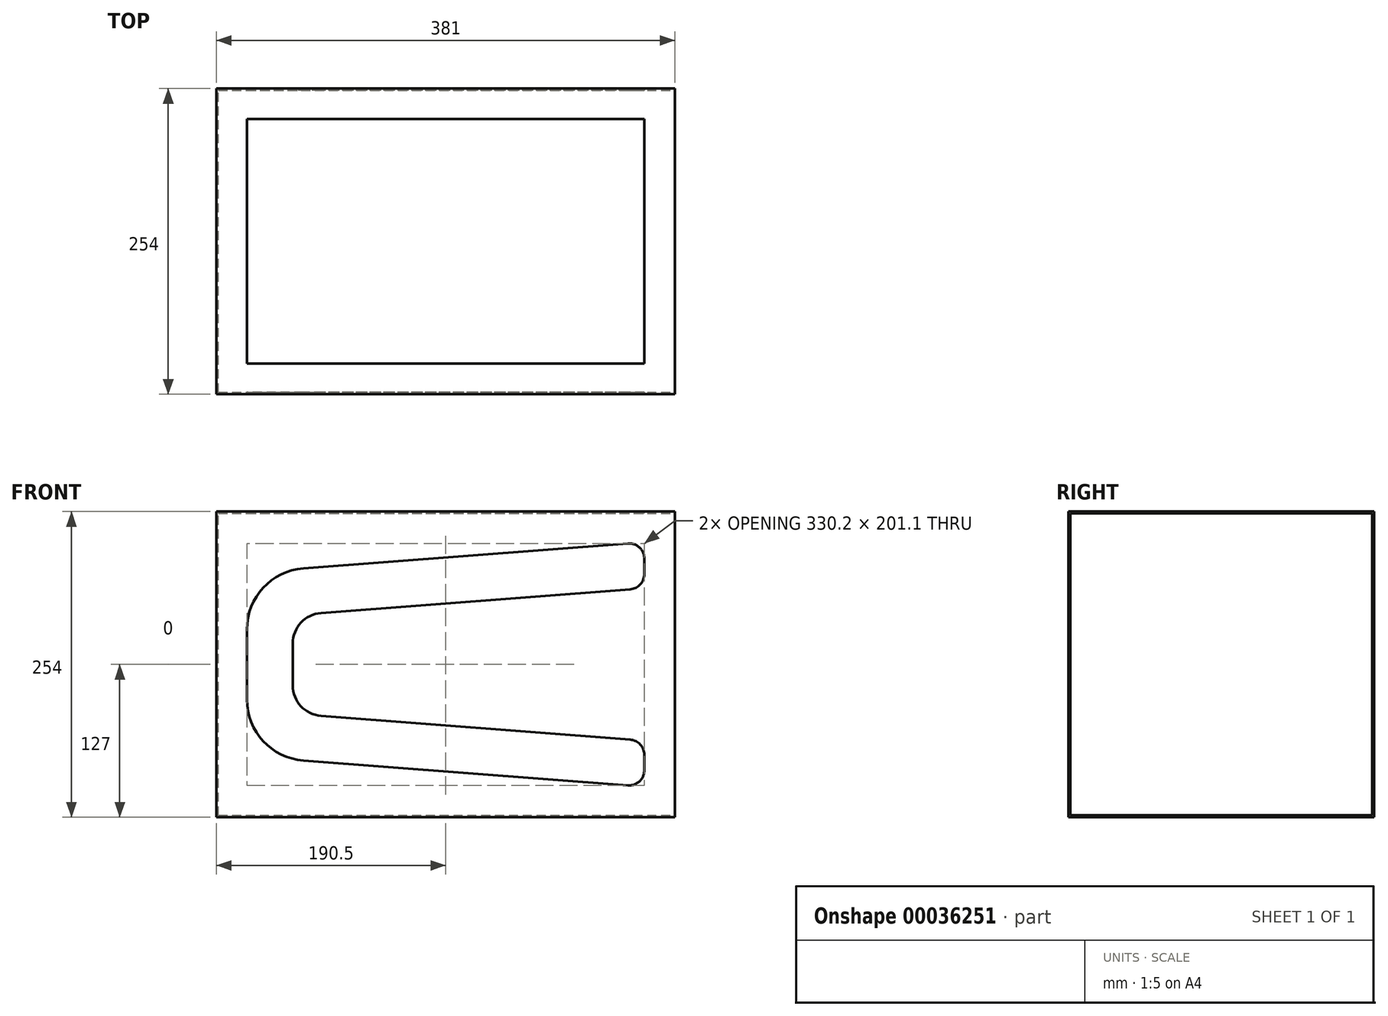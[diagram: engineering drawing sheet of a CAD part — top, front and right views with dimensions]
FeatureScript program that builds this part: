
annotation { "Feature Type Name" : "Feature", "Feature Type Description" : "" }
export const myFeature = defineFeature(function(context is Context, id is Id, definition is map)
    precondition{}
    {
        {
            var Q0;
            Q0=qCreatedBy(makeId("Front.planeOp"),FACE);
            var sketch = newSketch(context, id + "F0", { "sketchPlane" : qUnion([Q0])});
            skLineSegment(sketch, "E0.bottom", {"start": v(0, 0) * mm, "end": v(381, 0) * mm});
            skLineSegment(sketch, "E0.top", {"start": v(0, 254) * mm, "end": v(381, 254) * mm});
            skLineSegment(sketch, "E0.left", {"start": v(0, 0) * mm, "end": v(0, 254) * mm});
            skLineSegment(sketch, "E0.right", {"start": v(381, 0) * mm, "end": v(381, 254) * mm});
            skSolve(sketch);
        }
        {
            var Q0;
            Q0=qSketchRegion(id+"F0",true);
            extrude(context, id + "F1", {"entities" : qUnion([Q0]), "depth" : 254 * mm});
        }
        {
            var Q0;
            Q0=makeQuery(id+"F1.opExtrude","SWEPT_FACE",FACE,{"disambiguationData":[OSD([sQuery(id+"F0.wireOp",EDGE,"E0.right")])]});
            shell(context, id + "F2", {"entities" : qUnion([Q0]), "thickness" : 1.59 * mm});
        }
        {
            var Q0;
            Q0=makeQuery(id+"F1.opExtrude","CAP_FACE",FACE,{"disambiguationData":[OSD([sQuery(id+"F0.wireOp",EDGE,"E0.bottom"),sQuery(id+"F0.wireOp",EDGE,"E0.top"),sQuery(id+"F0.wireOp",EDGE,"E0.left"),sQuery(id+"F0.wireOp",EDGE,"E0.right")])],"isStart":false});
            var sketch = newSketch(context, id + "F3", { "sketchPlane" : qUnion([Q0])});
            skLineSegment(sketch, "E1.left", {"start": v(25.4, 97.84) * mm, "end": v(25.4, 156.16) * mm});
            skLineSegment(sketch, "E1.right", {"start": v(355.6, 39.11) * mm, "end": v(355.6, 51.85) * mm});
            skLineSegment(sketch, "E2", {"start": v(341.93, 227.55) * mm, "end": v(72.3, 206.8) * mm});
            skPoint(sketch, "E1.top.start.orphan", {"position": v(25.4, 228.6) * mm});
            skLineSegment(sketch, "E3.0", {"start": v(343.87, 189.49) * mm, "end": v(86.95, 169.72) * mm});
            skLineSegment(sketch, "E4", {"start": v(341.93, 26.45) * mm, "end": v(72.3, 47.2) * mm});
            skPoint(sketch, "E5.orphan", {"position": v(25.4, 25.4) * mm});
            skLineSegment(sketch, "E6.0", {"start": v(343.87, 64.51) * mm, "end": v(86.95, 84.28) * mm});
            skLineSegment(sketch, "E7.0", {"start": v(63.5, 109.6) * mm, "end": v(63.5, 144.4) * mm});
            skLineSegment(sketch, "E8.trimOffspring", {"start": v(355.6, 202.15) * mm, "end": v(355.6, 214.89) * mm});
            skPoint(sketch, "E9.visualSharp", {"position": v(25.4, 203.2) * mm});
            skArc(sketch, "E9.filletArc", {"start": v(72.3, 206.8) * mm, "mid": v(38.93, 190.67) * mm, "end": v(25.4, 156.16) * mm});
            skPoint(sketch, "E10.visualSharp", {"position": v(25.4, 50.8) * mm});
            skArc(sketch, "E10.filletArc", {"start": v(25.4, 97.84) * mm, "mid": v(38.93, 63.33) * mm, "end": v(72.3, 47.2) * mm});
            skPoint(sketch, "E11.visualSharp", {"position": v(63.5, 167.92) * mm});
            skArc(sketch, "E11.filletArc", {"start": v(86.95, 169.72) * mm, "mid": v(70.26, 161.66) * mm, "end": v(63.5, 144.4) * mm});
            skPoint(sketch, "E12.visualSharp", {"position": v(63.5, 86.08) * mm});
            skArc(sketch, "E12.filletArc", {"start": v(63.5, 109.6) * mm, "mid": v(70.26, 92.34) * mm, "end": v(86.95, 84.28) * mm});
            skPoint(sketch, "E13.visualSharp", {"position": v(355.6, 228.6) * mm});
            skArc(sketch, "E13.filletArc", {"start": v(355.6, 214.89) * mm, "mid": v(351.53, 224.2) * mm, "end": v(341.93, 227.55) * mm});
            skPoint(sketch, "E14.visualSharp", {"position": v(355.6, 190.39) * mm});
            skArc(sketch, "E14.filletArc", {"start": v(343.87, 189.49) * mm, "mid": v(352.22, 193.52) * mm, "end": v(355.6, 202.15) * mm});
            skPoint(sketch, "E15.visualSharp", {"position": v(355.6, 63.61) * mm});
            skArc(sketch, "E15.filletArc", {"start": v(355.6, 51.85) * mm, "mid": v(352.22, 60.48) * mm, "end": v(343.87, 64.51) * mm});
            skPoint(sketch, "E16.visualSharp", {"position": v(355.6, 25.4) * mm});
            skArc(sketch, "E16.filletArc", {"start": v(341.93, 26.45) * mm, "mid": v(351.53, 29.8) * mm, "end": v(355.6, 39.11) * mm});
            skSolve(sketch);
        }
        {
            var Q0;
            Q0=qSketchRegion(id+"F3",true);
            extrude(context, id + "F4", {"entities" : qUnion([Q0]), "operationType" : NewBodyOperationType.REMOVE, "endBound" : BoundingType.THROUGH_ALL, "oppositeDirection" : true, "depth" : 25.4 * mm});
        }
        {
            var Q0;
            Q0=makeQuery(id+"F1.opExtrude","SWEPT_FACE",FACE,{"disambiguationData":[OSD([sQuery(id+"F0.wireOp",EDGE,"E0.top")])]});
            var sketch = newSketch(context, id + "F5", { "sketchPlane" : qUnion([Q0])});
            skLineSegment(sketch, "E17.0", {"start": v(25.4, -25.4) * mm, "end": v(355.6, -25.4) * mm});
            skLineSegment(sketch, "E18.0", {"start": v(355.6, -228.6) * mm, "end": v(355.6, -25.4) * mm});
            skLineSegment(sketch, "E19.0", {"start": v(25.4, -228.6) * mm, "end": v(355.6, -228.6) * mm});
            skLineSegment(sketch, "E20.0", {"start": v(25.4, -228.6) * mm, "end": v(25.4, -25.4) * mm});
            skSolve(sketch);
        }
        {
            var Q0;
            Q0=qSketchRegion(id+"F5",true);
            extrude(context, id + "F6", {"entities" : qUnion([Q0]), "operationType" : NewBodyOperationType.REMOVE, "oppositeDirection" : true, "depth" : 25.4 * mm});
        }
    });
